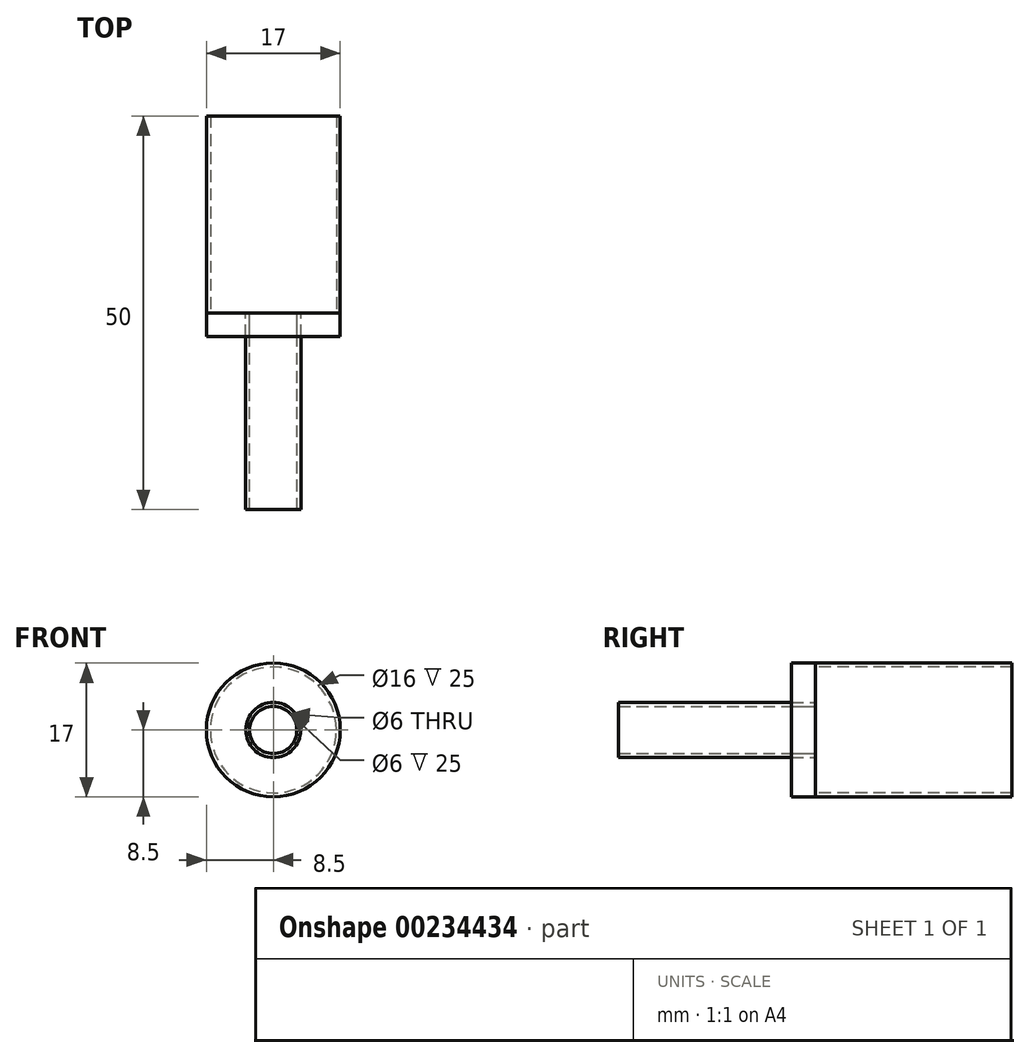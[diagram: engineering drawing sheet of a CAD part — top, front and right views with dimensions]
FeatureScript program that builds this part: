
annotation { "Feature Type Name" : "Feature", "Feature Type Description" : "" }
export const myFeature = defineFeature(function(context is Context, id is Id, definition is map)
    precondition{}
    {
        {
            var Q0;
            Q0=qCreatedBy(makeId("Front.planeOp"),FACE);
            var sketch = newSketch(context, id + "F0", { "sketchPlane" : qUnion([Q0])});
            skCircle(sketch, "E0", {"center": v(0, 0) * mm, "radius": 3.5 * mm});
            skCircle(sketch, "E1", {"center": v(0, 0) * mm, "radius": 3 * mm});
            skSolve(sketch);
        }
        {
            var Q0;
            Q0 = qSketchRegion(id + "F0", true);
            extrude(context, id + "F1", {"entities" : qUnion([Q0]), "depth" : 25 * mm});
        }
        {
            var Q0;
            Q0=qCreatedBy(makeId("Front.planeOp"),FACE);
            var sketch = newSketch(context, id + "F2", { "sketchPlane" : qUnion([Q0])});
            skCircle(sketch, "E2", {"center": v(0, 0) * mm, "radius": 8.5 * mm});
            skCircle(sketch, "E3", {"center": v(0, 0) * mm, "radius": 3 * mm});
            skSolve(sketch);
        }
        {
            var Q0;
            Q0 = qSketchRegion(id + "F2", true);
            extrude(context, id + "F3", {"entities" : qUnion([Q0]), "depth" : 3 * mm});
        }
        {
            var Q0;
            Q0=makeQuery(id+"F3.opExtrude","CAP_FACE",FACE,{"disambiguationData":[OSD([sQuery(id+"F2.wireOp",EDGE,"E2"),sQuery(id+"F2.wireOp",EDGE,"E3")])],"isStart":true});
            var sketch = newSketch(context, id + "F4", { "sketchPlane" : qUnion([Q0])});
            skCircle(sketch, "E4.0", {"center": v(0, 0) * mm, "radius": 8 * mm});
            skCircle(sketch, "E5", {"center": v(0, 0) * mm, "radius": 8.5 * mm});
            skSolve(sketch);
        }
        {
            var Q0;
            Q0 = qSketchRegion(id + "F4", true);
            extrude(context, id + "F5", {"entities" : qUnion([Q0]), "depth" : 25 * mm});
        }
    });
